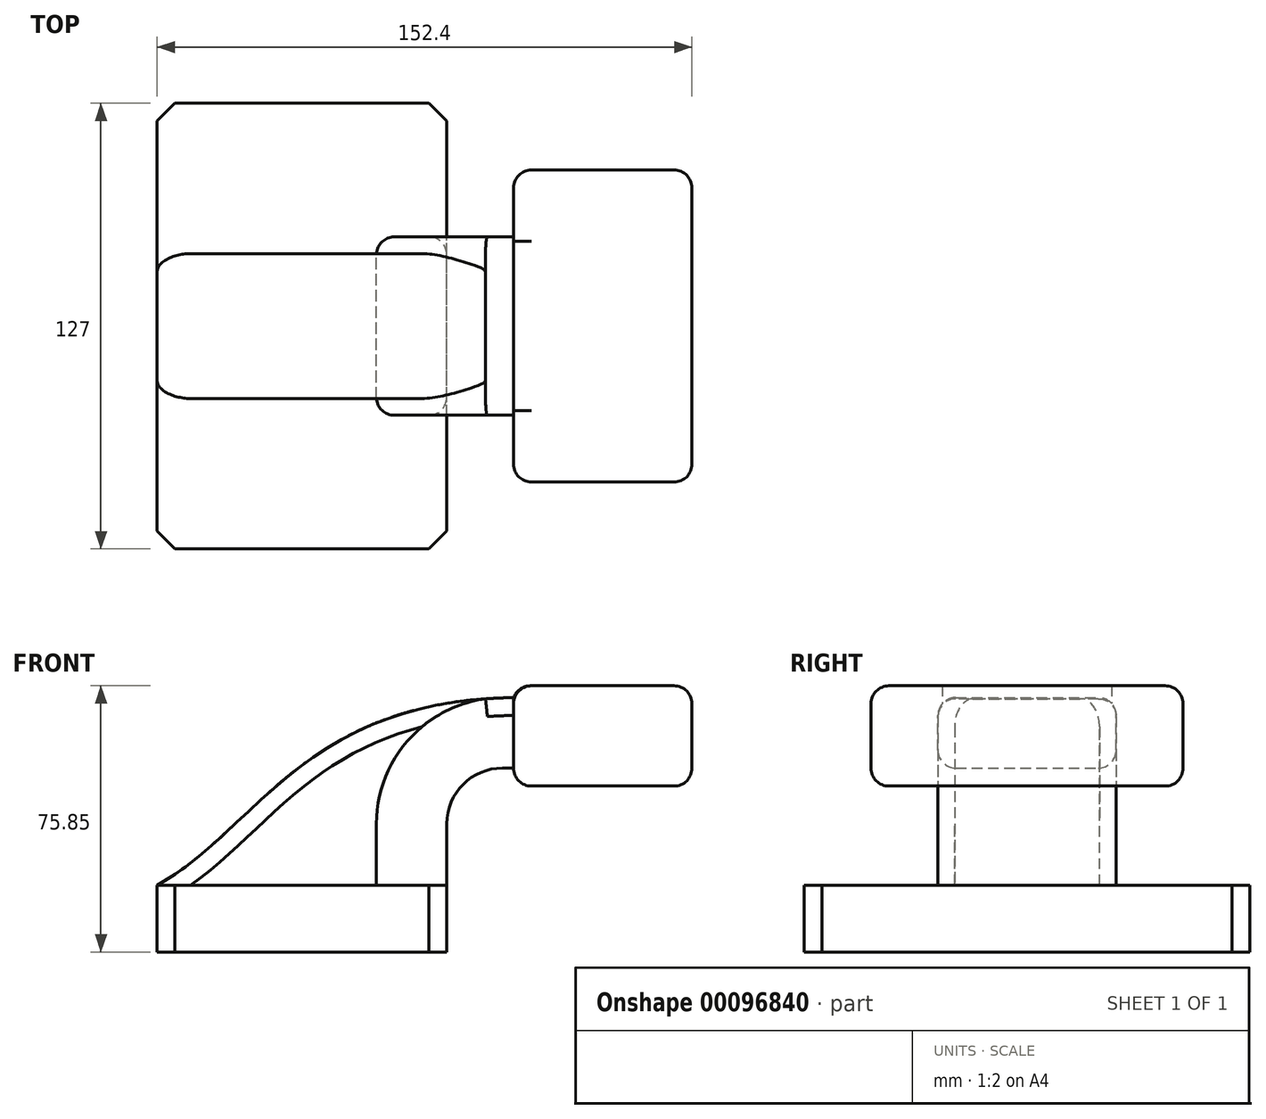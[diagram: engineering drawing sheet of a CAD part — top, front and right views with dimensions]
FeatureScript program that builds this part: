
annotation { "Feature Type Name" : "Feature", "Feature Type Description" : "" }
export const myFeature = defineFeature(function(context is Context, id is Id, definition is map)
    precondition{}
    {
        {
            var Q0;
            Q0=qCreatedBy(makeId("Front.planeOp"),FACE);
            var sketch = newSketch(context, id + "F0", { "sketchPlane" : qUnion([Q0])});
            skLineSegment(sketch, "E0.bottom", {"start": v(41.28, -9.52) * mm, "end": v(-41.27, -9.52) * mm});
            skLineSegment(sketch, "E0.top", {"start": v(41.27, 9.53) * mm, "end": v(-41.28, 9.53) * mm});
            skLineSegment(sketch, "E0.left", {"start": v(41.28, -9.52) * mm, "end": v(41.28, 9.53) * mm});
            skLineSegment(sketch, "E0.right", {"start": v(-41.27, -9.52) * mm, "end": v(-41.28, 9.53) * mm});
            skPoint(sketch, "E0.middle", {"position": v(0, 0) * mm});
            skLineSegment(sketch, "E1.bottom", {"start": v(111.13, 37.74) * mm, "end": v(60.33, 37.74) * mm});
            skLineSegment(sketch, "E1.top", {"start": v(111.13, 66.32) * mm, "end": v(60.33, 66.32) * mm});
            skLineSegment(sketch, "E1.left", {"start": v(111.13, 37.74) * mm, "end": v(111.13, 66.32) * mm});
            skLineSegment(sketch, "E1.right", {"start": v(60.33, 37.74) * mm, "end": v(60.33, 66.32) * mm});
            skPoint(sketch, "E1.middle", {"position": v(85.73, 52.03) * mm});
            skLineSegment(sketch, "E2", {"start": v(41.27, 9.53) * mm, "end": v(41.27, 27) * mm});
            skArc(sketch, "E3", {"start": v(41.27, 27) * mm, "mid": v(45.92, 38.23) * mm, "end": v(57.15, 42.88) * mm});
            skLineSegment(sketch, "E4", {"start": v(57.15, 42.88) * mm, "end": v(85.83, 42.88) * mm});
            skLineSegment(sketch, "E5.0", {"start": v(57.15, 62.94) * mm, "end": v(85.83, 62.94) * mm});
            skArc(sketch, "E5.1", {"start": v(21.2, 27) * mm, "mid": v(31.74, 52.41) * mm, "end": v(57.15, 62.94) * mm});
            skLineSegment(sketch, "E5.2", {"start": v(21.2, 9.53) * mm, "end": v(21.2, 27) * mm});
            skLineSegment(sketch, "E6", {"start": v(85.83, 66.32) * mm, "end": v(85.83, 37.74) * mm});
            skFitSpline(sketch, "E7", {"points": [v(-41.28, 9.53) * mm, v(60.33, 62.94) * mm], "startDerivative": vector(85.02, 46.43) * mm, "endDerivative": vector(180.98, 2.24) * mm});
            skSolve(sketch);
        }
        {
            var Q0;
            Q0=makeQuery(id+"F0.imprint","IMPRINT",FACE,{"disambiguationData":[TD([[makeQuery(id+"F0.imprint","IMPRINT",EDGE,{"derivedFrom":sQuery(id+"F0.wireOp",EDGE,"E0.bottom")}),-1.0]])]});
            extrude(context, id + "F1", {"entities" : qUnion([Q0]), "endBound" : BoundingType.SYMMETRIC, "depth" : 127 * mm});
        }
        {
            var Q0;
            {var subQ1=sQuery(id+"F0.wireOp",EDGE,"E2");Q0=makeQuery(id+"F0.imprint","IMPRINT",FACE,{"disambiguationData":[TD([[makeQuery(id+"F0.imprint","IMPRINT",EDGE,{"derivedFrom":subQ1}),1.0]])]});}
            extrude(context, id + "F2", {"entities" : qUnion([Q0]), "endBound" : BoundingType.SYMMETRIC, "depth" : 50.8 * mm});
        }
        {
            var Q0;
            {var subQ3=sQuery(id+"F0.wireOp",EDGE,"E5.2");Q0=makeQuery(id+"F0.imprint","IMPRINT",FACE,{"disambiguationData":[TD([[makeQuery(id+"F0.imprint","IMPRINT",EDGE,{"derivedFrom":subQ3}),1.0]])]});}
            extrude(context, id + "F3", {"entities" : qUnion([Q0]), "endBound" : BoundingType.SYMMETRIC, "depth" : 41.27 * mm});
        }
        {
            var Q0;
            {var subQ3=sQuery(id+"F0.wireOp",EDGE,"E4");var subQ5=sQuery(id+"F0.wireOp",EDGE,"E6");var subQ6=makeQuery(id+"F0.imprint","INTERSECT",VERTEX,{"derivedFrom":[subQ3,subQ5]});Q0=makeQuery(id+"F0.imprint","IMPRINT",FACE,{"disambiguationData":[TD([[makeQuery(id+"F0.imprint","IMPRINT",EDGE,{"disambiguationData":[TD([[subQ6,1.0]])],"derivedFrom":subQ3}),1.0]])]});}
            var Q1;
            {var subQ0=sQuery(id+"F0.wireOp",EDGE,"E1.right");var subQ1=sQuery(id+"F0.wireOp",EDGE,"E1.top");var subQ2=makeQuery(id+"F0.imprint","INTERSECT",VERTEX,{"derivedFrom":[subQ1,subQ0]});Q1=makeQuery(id+"F0.imprint","IMPRINT",FACE,{"disambiguationData":[TD([[makeQuery(id+"F0.imprint","IMPRINT",EDGE,{"disambiguationData":[TD([[subQ2,1.0]])],"derivedFrom":subQ1}),1.0]])]});}
            var Q2;
            {var subQ0=sQuery(id+"F0.wireOp",EDGE,"E1.right");var subQ1=sQuery(id+"F0.wireOp",EDGE,"E1.bottom");var subQ2=makeQuery(id+"F0.imprint","INTERSECT",VERTEX,{"derivedFrom":[subQ1,subQ0]});Q2=makeQuery(id+"F0.imprint","IMPRINT",FACE,{"disambiguationData":[TD([[makeQuery(id+"F0.imprint","IMPRINT",EDGE,{"disambiguationData":[TD([[subQ2,1.0]])],"derivedFrom":subQ1}),-1.0]])]});}
            var Q3;
            {var subQ0=sQuery(id+"F0.wireOp",EDGE,"E1.left");Q3=makeQuery(id+"F0.imprint","IMPRINT",FACE,{"disambiguationData":[TD([[makeQuery(id+"F0.imprint","IMPRINT",EDGE,{"derivedFrom":subQ0}),1.0]])]});}
            extrude(context, id + "F4", {"entities" : qUnion([Q0, Q1, Q2, Q3]), "operationType" : NewBodyOperationType.ADD, "endBound" : BoundingType.SYMMETRIC, "depth" : 88.9 * mm});
        }
        {
            var Q0;
            Q0=makeQuery(id+"F1.opExtrude","CAP_EDGE",EDGE,{"disambiguationData":[OSD([sQuery(id+"F0.wireOp",EDGE,"E0.right")])],"isStart":false});
            var Q1;
            Q1=makeQuery(id+"F1.opExtrude","CAP_EDGE",EDGE,{"disambiguationData":[OSD([sQuery(id+"F0.wireOp",EDGE,"E0.left")])],"isStart":false});
            var Q2;
            Q2=makeQuery(id+"F1.opExtrude","CAP_EDGE",EDGE,{"disambiguationData":[OSD([sQuery(id+"F0.wireOp",EDGE,"E0.right")])],"isStart":true});
            var Q3;
            Q3=makeQuery(id+"F1.opExtrude","CAP_EDGE",EDGE,{"disambiguationData":[OSD([sQuery(id+"F0.wireOp",EDGE,"E0.left")])],"isStart":true});
            chamfer(context, id + "F5", {"entities" : qUnion([Q0, Q1, Q2, Q3]), "width" : 5.08 * mm, "tangentPropagation" : true});
        }
        {
            var Q0;
            Q0=makeQuery(id+"F4.opExtrude","CAP_EDGE",EDGE,{"disambiguationData":[OSD([sQuery(id+"F0.wireOp",EDGE,"E1.right")])],"isStart":true});
            var Q1;
            Q1=makeQuery(id+"F4.opExtrude","CAP_EDGE",EDGE,{"disambiguationData":[OSD([sQuery(id+"F0.wireOp",EDGE,"E1.left")])],"isStart":true});
            var Q2;
            Q2=makeQuery(id+"F4.opExtrude","CAP_EDGE",EDGE,{"disambiguationData":[OSD([sQuery(id+"F0.wireOp",EDGE,"E1.left")])],"isStart":false});
            var Q3;
            Q3=makeQuery(id+"F4.opExtrude","CAP_EDGE",EDGE,{"disambiguationData":[OSD([sQuery(id+"F0.wireOp",EDGE,"E1.right")])],"isStart":false});
            fillet(context, id + "F6", {"entities" : qUnion([Q0, Q1, Q2, Q3]), "radius" : 5.08 * mm, "tangentPropagation" : true, "allowEdgeOverflow" : false});
        }
        {
            var Q0;
            Q0=makeQuery(id+"F3.opExtrude","CAP_EDGE",EDGE,{"disambiguationData":[OSD([sQuery(id+"F0.wireOp",EDGE,"E7")])],"isStart":false});
            fillet(context, id + "F7", {"entities" : qUnion([Q0]), "radius" : 5.08 * mm, "tangentPropagation" : true, "allowEdgeOverflow" : false});
        }
        {
            var Q0;
            Q0=makeQuery(id+"F3.opExtrude","CAP_EDGE",EDGE,{"disambiguationData":[OSD([sQuery(id+"F0.wireOp",EDGE,"E7")])],"isStart":true});
            fillet(context, id + "F8", {"entities" : qUnion([Q0]), "radius" : 5.08 * mm, "tangentPropagation" : true, "allowEdgeOverflow" : false});
        }
        {
            var Q0;
            Q0=makeQuery(id+"F2.opExtrude","CAP_EDGE",EDGE,{"disambiguationData":[OSD([sQuery(id+"F0.wireOp",EDGE,"E5.1")])],"isStart":false});
            var Q1;
            Q1=makeQuery(id+"F2.opExtrude","CAP_EDGE",EDGE,{"disambiguationData":[OSD([sQuery(id+"F0.wireOp",EDGE,"E7")])],"isStart":false});
            var Q2;
            Q2=makeQuery(id+"F2.opExtrude","CAP_EDGE",EDGE,{"disambiguationData":[OSD([sQuery(id+"F0.wireOp",EDGE,"E5.2")])],"isStart":false});
            fillet(context, id + "F9", {"entities" : qUnion([Q0, Q1, Q2]), "radius" : 5.08 * mm, "tangentPropagation" : true, "allowEdgeOverflow" : false});
        }
        {
            var Q0;
            Q0=makeQuery(id+"F2.opExtrude","CAP_EDGE",EDGE,{"disambiguationData":[OSD([sQuery(id+"F0.wireOp",EDGE,"E5.1")])],"isStart":true});
            var Q1;
            Q1=makeQuery(id+"F2.opExtrude","CAP_EDGE",EDGE,{"disambiguationData":[OSD([sQuery(id+"F0.wireOp",EDGE,"E5.2")])],"isStart":true});
            var Q2;
            Q2=makeQuery(id+"F2.opExtrude","CAP_EDGE",EDGE,{"disambiguationData":[OSD([sQuery(id+"F0.wireOp",EDGE,"E7")])],"isStart":true});
            var Q3;
            Q3=makeQuery(id+"F2.opExtrude","CAP_EDGE",EDGE,{"disambiguationData":[OSD([sQuery(id+"F0.wireOp",EDGE,"E4")])],"isStart":true});
            var Q4;
            Q4=makeQuery(id+"F2.opExtrude","CAP_EDGE",EDGE,{"disambiguationData":[OSD([sQuery(id+"F0.wireOp",EDGE,"E3")])],"isStart":true});
            var Q5;
            Q5=makeQuery(id+"F2.opExtrude","CAP_EDGE",EDGE,{"disambiguationData":[OSD([sQuery(id+"F0.wireOp",EDGE,"E2")])],"isStart":true});
            var Q6;
            Q6=makeQuery(id+"F2.opExtrude","CAP_EDGE",EDGE,{"disambiguationData":[OSD([sQuery(id+"F0.wireOp",EDGE,"E2")])],"isStart":false});
            var Q7;
            Q7=makeQuery(id+"F2.opExtrude","CAP_EDGE",EDGE,{"disambiguationData":[OSD([sQuery(id+"F0.wireOp",EDGE,"E3")])],"isStart":false});
            fillet(context, id + "F10", {"entities" : qUnion([Q0, Q1, Q2, Q3, Q4, Q5, Q6, Q7]), "radius" : 5.08 * mm, "tangentPropagation" : true, "allowEdgeOverflow" : false});
        }
        {
            var Q0;
            Q0=makeQuery(id+"F4.opExtrude","CAP_EDGE",EDGE,{"disambiguationData":[OSD([sQuery(id+"F0.wireOp",EDGE,"E1.top")])],"isStart":false});
            var Q1;
            Q1=makeQuery(id+"F6.opFillet","BLEND_EDGE",EDGE,{"blendedFrom":[makeQuery(id+"F4.opExtrude","CAP_EDGE",EDGE,{"disambiguationData":[OSD([sQuery(id+"F0.wireOp",EDGE,"E1.left")])],"isStart":false}),makeQuery(id+"F4.opExtrude","SWEPT_FACE",FACE,{"disambiguationData":[OSD([sQuery(id+"F0.wireOp",EDGE,"E1.top")])]})],"blendedInto":[makeQuery(id+"F4.opExtrude","SWEPT_FACE",FACE,{"disambiguationData":[OSD([sQuery(id+"F0.wireOp",EDGE,"E1.top")])]})]});
            var Q2;
            Q2=makeQuery(id+"F4.opExtrude","SWEPT_EDGE",EDGE,{"disambiguationData":[OSD([sQuery(id+"F0.wireOp",EDGE,"E1.top"),sQuery(id+"F0.wireOp",EDGE,"E1.left")])]});
            var Q3;
            Q3=makeQuery(id+"F6.opFillet","BLEND_EDGE",EDGE,{"blendedFrom":[makeQuery(id+"F4.opExtrude","CAP_EDGE",EDGE,{"disambiguationData":[OSD([sQuery(id+"F0.wireOp",EDGE,"E1.left")])],"isStart":true}),makeQuery(id+"F4.opExtrude","SWEPT_FACE",FACE,{"disambiguationData":[OSD([sQuery(id+"F0.wireOp",EDGE,"E1.top")])]})],"blendedInto":[makeQuery(id+"F4.opExtrude","SWEPT_FACE",FACE,{"disambiguationData":[OSD([sQuery(id+"F0.wireOp",EDGE,"E1.top")])]})]});
            var Q4;
            Q4=makeQuery(id+"F4.opExtrude","CAP_EDGE",EDGE,{"disambiguationData":[OSD([sQuery(id+"F0.wireOp",EDGE,"E1.top")])],"isStart":true});
            var Q5;
            Q5=makeQuery(id+"F4.opExtrude","SWEPT_EDGE",EDGE,{"disambiguationData":[OSD([sQuery(id+"F0.wireOp",EDGE,"E1.top"),sQuery(id+"F0.wireOp",EDGE,"E1.right")])]});
            var Q6;
            Q6=makeQuery(id+"F6.opFillet","BLEND_EDGE",EDGE,{"blendedFrom":[makeQuery(id+"F4.opExtrude","CAP_EDGE",EDGE,{"disambiguationData":[OSD([sQuery(id+"F0.wireOp",EDGE,"E1.right")])],"isStart":false}),makeQuery(id+"F4.opExtrude","SWEPT_FACE",FACE,{"disambiguationData":[OSD([sQuery(id+"F0.wireOp",EDGE,"E1.top")])]})],"blendedInto":[makeQuery(id+"F4.opExtrude","SWEPT_FACE",FACE,{"disambiguationData":[OSD([sQuery(id+"F0.wireOp",EDGE,"E1.top")])]})]});
            var Q7;
            Q7=makeQuery(id+"F6.opFillet","BLEND_EDGE",EDGE,{"blendedFrom":[makeQuery(id+"F4.opExtrude","CAP_EDGE",EDGE,{"disambiguationData":[OSD([sQuery(id+"F0.wireOp",EDGE,"E1.right")])],"isStart":true}),makeQuery(id+"F4.opExtrude","SWEPT_FACE",FACE,{"disambiguationData":[OSD([sQuery(id+"F0.wireOp",EDGE,"E1.top")])]})],"blendedInto":[makeQuery(id+"F4.opExtrude","SWEPT_FACE",FACE,{"disambiguationData":[OSD([sQuery(id+"F0.wireOp",EDGE,"E1.top")])]})]});
            var Q8;
            Q8=makeQuery(id+"F4.opExtrude","CAP_EDGE",EDGE,{"disambiguationData":[OSD([sQuery(id+"F0.wireOp",EDGE,"E1.bottom")])],"isStart":true});
            var Q9;
            Q9=makeQuery(id+"F6.opFillet","BLEND_EDGE",EDGE,{"blendedFrom":[makeQuery(id+"F4.opExtrude","CAP_EDGE",EDGE,{"disambiguationData":[OSD([sQuery(id+"F0.wireOp",EDGE,"E1.right")])],"isStart":true}),makeQuery(id+"F4.opExtrude","SWEPT_FACE",FACE,{"disambiguationData":[OSD([sQuery(id+"F0.wireOp",EDGE,"E1.bottom")])]})],"blendedInto":[makeQuery(id+"F4.opExtrude","SWEPT_FACE",FACE,{"disambiguationData":[OSD([sQuery(id+"F0.wireOp",EDGE,"E1.bottom")])]})]});
            var Q10;
            Q10=makeQuery(id+"F4.opExtrude","SWEPT_EDGE",EDGE,{"disambiguationData":[OSD([sQuery(id+"F0.wireOp",EDGE,"E1.bottom"),sQuery(id+"F0.wireOp",EDGE,"E1.right")])]});
            var Q11;
            Q11=makeQuery(id+"F6.opFillet","BLEND_EDGE",EDGE,{"blendedFrom":[makeQuery(id+"F4.opExtrude","CAP_EDGE",EDGE,{"disambiguationData":[OSD([sQuery(id+"F0.wireOp",EDGE,"E1.left")])],"isStart":true}),makeQuery(id+"F4.opExtrude","SWEPT_FACE",FACE,{"disambiguationData":[OSD([sQuery(id+"F0.wireOp",EDGE,"E1.bottom")])]})],"blendedInto":[makeQuery(id+"F4.opExtrude","SWEPT_FACE",FACE,{"disambiguationData":[OSD([sQuery(id+"F0.wireOp",EDGE,"E1.bottom")])]})]});
            var Q12;
            Q12=makeQuery(id+"F4.opExtrude","SWEPT_EDGE",EDGE,{"disambiguationData":[OSD([sQuery(id+"F0.wireOp",EDGE,"E1.bottom"),sQuery(id+"F0.wireOp",EDGE,"E1.left")])]});
            var Q13;
            Q13=makeQuery(id+"F4.opExtrude","CAP_EDGE",EDGE,{"disambiguationData":[OSD([sQuery(id+"F0.wireOp",EDGE,"E1.bottom")])],"isStart":false});
            var Q14;
            Q14=makeQuery(id+"F6.opFillet","BLEND_EDGE",EDGE,{"blendedFrom":[makeQuery(id+"F4.opExtrude","CAP_EDGE",EDGE,{"disambiguationData":[OSD([sQuery(id+"F0.wireOp",EDGE,"E1.right")])],"isStart":false}),makeQuery(id+"F4.opExtrude","SWEPT_FACE",FACE,{"disambiguationData":[OSD([sQuery(id+"F0.wireOp",EDGE,"E1.bottom")])]})],"blendedInto":[makeQuery(id+"F4.opExtrude","SWEPT_FACE",FACE,{"disambiguationData":[OSD([sQuery(id+"F0.wireOp",EDGE,"E1.bottom")])]})]});
            var Q15;
            Q15=makeQuery(id+"F6.opFillet","BLEND_EDGE",EDGE,{"blendedFrom":[makeQuery(id+"F4.opExtrude","CAP_EDGE",EDGE,{"disambiguationData":[OSD([sQuery(id+"F0.wireOp",EDGE,"E1.left")])],"isStart":false}),makeQuery(id+"F4.opExtrude","SWEPT_FACE",FACE,{"disambiguationData":[OSD([sQuery(id+"F0.wireOp",EDGE,"E1.bottom")])]})],"blendedInto":[makeQuery(id+"F4.opExtrude","SWEPT_FACE",FACE,{"disambiguationData":[OSD([sQuery(id+"F0.wireOp",EDGE,"E1.bottom")])]})]});
            fillet(context, id + "F11", {"entities" : qUnion([Q0, Q1, Q2, Q3, Q4, Q5, Q6, Q7, Q8, Q9, Q10, Q11, Q12, Q13, Q14, Q15]), "radius" : 5.08 * mm, "tangentPropagation" : true, "allowEdgeOverflow" : false});
        }
    });
